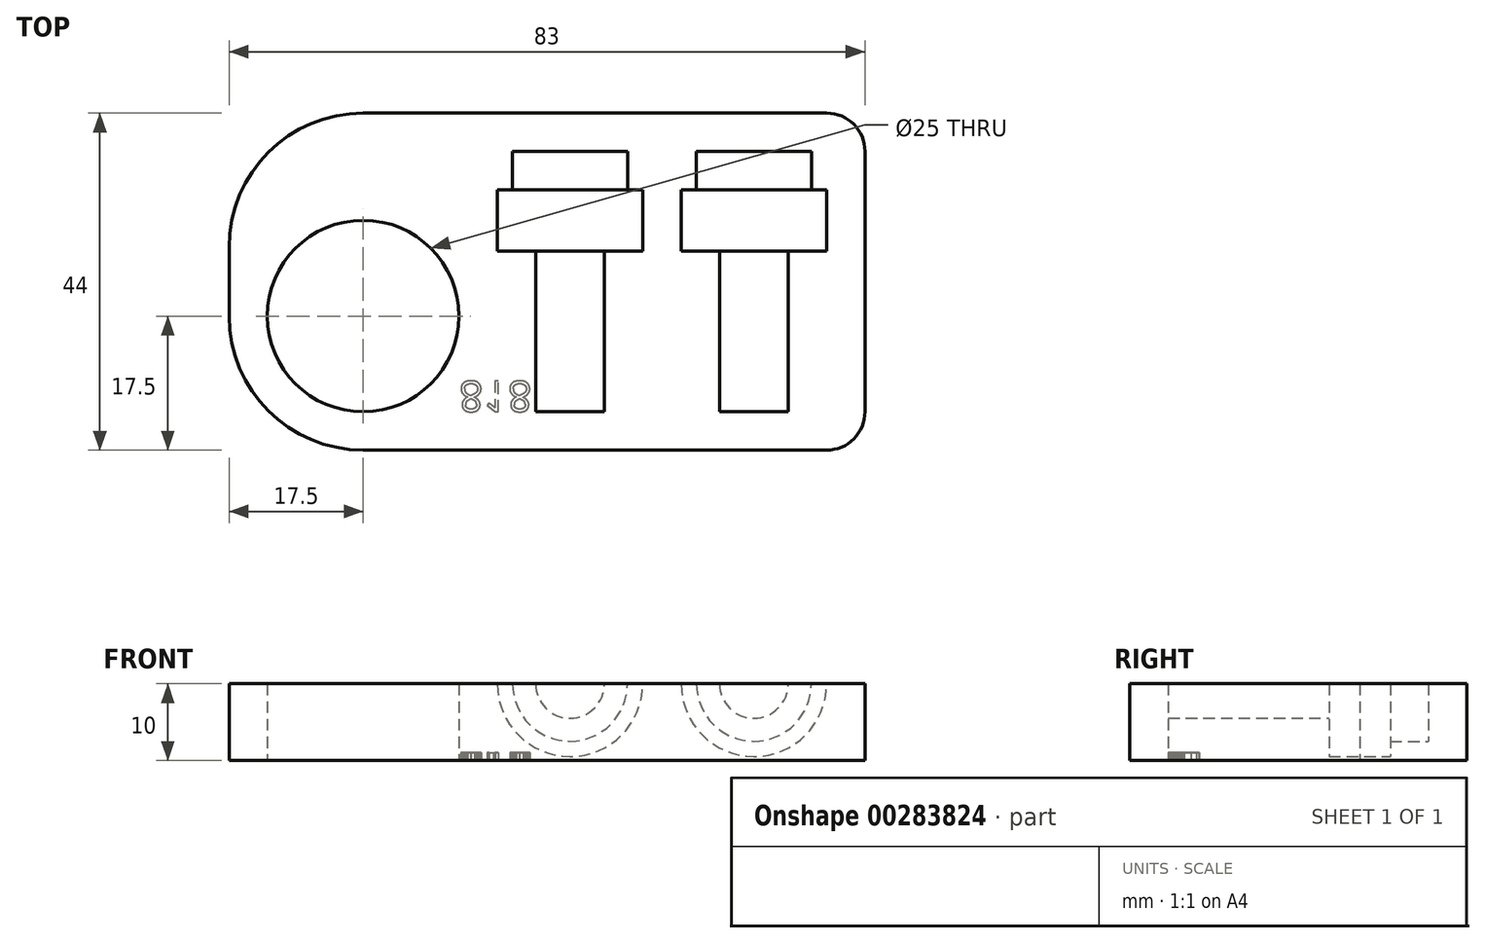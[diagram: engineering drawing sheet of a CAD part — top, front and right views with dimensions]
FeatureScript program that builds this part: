
annotation { "Feature Type Name" : "Feature", "Feature Type Description" : "" }
export const myFeature = defineFeature(function(context is Context, id is Id, definition is map)
    precondition{}
    {
        {
            var Q0;
            Q0=qCreatedBy(makeId("Top.planeOp"),FACE);
            var sketch = newSketch(context, id + "F0", { "sketchPlane" : qUnion([Q0])});
            skLineSegment(sketch, "E0.bottom", {"start": v(17.5, 0) * mm, "end": v(78, 0) * mm});
            skLineSegment(sketch, "E0.top", {"start": v(17.5, 44) * mm, "end": v(78, 44) * mm});
            skLineSegment(sketch, "E0.left", {"start": v(0, 17.5) * mm, "end": v(0, 26.5) * mm});
            skLineSegment(sketch, "E0.right", {"start": v(83, 5) * mm, "end": v(83, 39) * mm});
            skLineSegment(sketch, "E1.bottom", {"start": v(0, 0) * mm, "end": v(17.5, 0) * mm, "construction": true});
            skLineSegment(sketch, "E1.top", {"start": v(0, 17.5) * mm, "end": v(17.5, 17.5) * mm, "construction": true});
            skLineSegment(sketch, "E1.left", {"start": v(0, 0) * mm, "end": v(0, 17.5) * mm, "construction": true});
            skLineSegment(sketch, "E1.right", {"start": v(17.5, 0) * mm, "end": v(17.5, 17.5) * mm, "construction": true});
            skCircle(sketch, "E2", {"center": v(17.5, 17.5) * mm, "radius": 12.5 * mm});
            skPoint(sketch, "E3.visualSharp", {"position": v(0, 0) * mm});
            skArc(sketch, "E3.filletArc", {"start": v(0, 17.5) * mm, "mid": v(5.13, 5.13) * mm, "end": v(17.5, 0) * mm});
            skPoint(sketch, "E4.visualSharp", {"position": v(0, 44) * mm});
            skArc(sketch, "E4.filletArc", {"start": v(17.5, 44) * mm, "mid": v(5.13, 38.87) * mm, "end": v(0, 26.5) * mm});
            skPoint(sketch, "E5.visualSharp", {"position": v(83, 44) * mm});
            skArc(sketch, "E5.filletArc", {"start": v(83, 39) * mm, "mid": v(81.54, 42.54) * mm, "end": v(78, 44) * mm});
            skPoint(sketch, "E6.visualSharp", {"position": v(83, 0) * mm});
            skArc(sketch, "E6.filletArc", {"start": v(78, 0) * mm, "mid": v(81.54, 1.46) * mm, "end": v(83, 5) * mm});
            skSolve(sketch);
        }
        {
            var Q0;
            Q0=makeQuery(id+"F0.imprint","IMPRINT",FACE,{"disambiguationData":[TD([[makeQuery(id+"F0.imprint","IMPRINT",EDGE,{"derivedFrom":sQuery(id+"F0.wireOp",EDGE,"E0.bottom")}),1.0]])]});
            extrude(context, id + "F1", {"entities" : qUnion([Q0]), "depth" : 10 * mm});
        }
        {
            var Q0;
            Q0=makeQuery(id+"F1.opExtrude","CAP_FACE",FACE,{"disambiguationData":[OSD([sQuery(id+"F0.wireOp",EDGE,"E0.bottom"),sQuery(id+"F0.wireOp",EDGE,"E0.top"),sQuery(id+"F0.wireOp",EDGE,"E0.right"),sQuery(id+"F0.wireOp",EDGE,"E2"),sQuery(id+"F0.wireOp",EDGE,"E3.filletArc"),sQuery(id+"F0.wireOp",EDGE,"E4.filletArc"),sQuery(id+"F0.wireOp",EDGE,"E5.filletArc"),sQuery(id+"F0.wireOp",EDGE,"E6.filletArc")])],"isStart":false});
            var sketch = newSketch(context, id + "F2", { "sketchPlane" : qUnion([Q0])});
            skLineSegment(sketch, "E7.bottom", {"start": v(0, 0) * mm, "end": v(44.5, 0) * mm, "construction": true});
            skLineSegment(sketch, "E7.top", {"start": v(0, 5) * mm, "end": v(44.5, 5) * mm, "construction": true});
            skLineSegment(sketch, "E7.left", {"start": v(0, 0) * mm, "end": v(0, 5) * mm, "construction": true});
            skLineSegment(sketch, "E7.right", {"start": v(44.5, 0) * mm, "end": v(44.5, 5) * mm, "construction": true});
            skLineSegment(sketch, "E8.bottom", {"start": v(44.5, 5) * mm, "end": v(49, 5) * mm});
            skLineSegment(sketch, "E8.left", {"start": v(44.5, 5) * mm, "end": v(44.5, 26) * mm});
            skLineSegment(sketch, "E8.right", {"start": v(49, 5) * mm, "end": v(49, 26) * mm});
            skLineSegment(sketch, "E9.bottom", {"start": v(49, 26) * mm, "end": v(54, 26) * mm});
            skLineSegment(sketch, "E9.top", {"start": v(52, 34) * mm, "end": v(54, 34) * mm});
            skLineSegment(sketch, "E9.left", {"start": v(44.5, 26) * mm, "end": v(44.5, 34) * mm});
            skLineSegment(sketch, "E9.right", {"start": v(54, 26) * mm, "end": v(54, 34) * mm});
            skLineSegment(sketch, "E10.top", {"start": v(44.5, 39) * mm, "end": v(52, 39) * mm});
            skLineSegment(sketch, "E10.left", {"start": v(44.5, 34) * mm, "end": v(44.5, 39) * mm});
            skLineSegment(sketch, "E10.right", {"start": v(52, 34) * mm, "end": v(52, 39) * mm});
            skLineSegment(sketch, "E11", {"start": v(44.5, 5) * mm, "end": v(68.5, 5) * mm, "construction": true});
            skLineSegment(sketch, "E12.bottom", {"start": v(68.5, 5) * mm, "end": v(73, 5) * mm});
            skLineSegment(sketch, "E12.left", {"start": v(68.5, 5) * mm, "end": v(68.5, 26) * mm});
            skLineSegment(sketch, "E12.right", {"start": v(73, 5) * mm, "end": v(73, 26) * mm});
            skLineSegment(sketch, "E13.bottom", {"start": v(73, 26) * mm, "end": v(78, 26) * mm});
            skLineSegment(sketch, "E13.top", {"start": v(76, 34) * mm, "end": v(78, 34) * mm});
            skLineSegment(sketch, "E13.left", {"start": v(68.5, 26) * mm, "end": v(68.5, 34) * mm});
            skLineSegment(sketch, "E13.right", {"start": v(78, 26) * mm, "end": v(78, 34) * mm});
            skLineSegment(sketch, "E14.top", {"start": v(68.5, 39) * mm, "end": v(76, 39) * mm});
            skLineSegment(sketch, "E14.left", {"start": v(68.5, 34) * mm, "end": v(68.5, 39) * mm});
            skLineSegment(sketch, "E14.right", {"start": v(76, 34) * mm, "end": v(76, 39) * mm});
            skSolve(sketch);
        }
        {
            var Q0;
            Q0=makeQuery(id+"F2.imprint","IMPRINT",FACE,{"disambiguationData":[TD([[makeQuery(id+"F2.imprint","IMPRINT",EDGE,{"derivedFrom":sQuery(id+"F2.wireOp",EDGE,"E8.bottom")}),1.0]])]});
            var Q1;
            Q1=sQuery(id+"F2.wireOp",EDGE,"E8.left");
            revolve(context, id + "F3", {"operationType" : NewBodyOperationType.REMOVE, "entities" : qUnion([Q0]), "axis" : qUnion([Q1]), "revolveType" : RevolveType.FULL, "oppositeDirection" : true});
        }
        {
            var Q0;
            Q0=makeQuery(id+"F2.imprint","IMPRINT",FACE,{"disambiguationData":[TD([[makeQuery(id+"F2.imprint","IMPRINT",EDGE,{"derivedFrom":sQuery(id+"F2.wireOp",EDGE,"E12.bottom")}),1.0]])]});
            var Q1;
            Q1=sQuery(id+"F2.wireOp",EDGE,"E12.left");
            revolve(context, id + "F4", {"operationType" : NewBodyOperationType.REMOVE, "entities" : qUnion([Q0]), "axis" : qUnion([Q1]), "revolveType" : RevolveType.FULL, "oppositeDirection" : true});
        }
        {
            var Q0;
            Q0=makeQuery(id+"F1.opExtrude","CAP_FACE",FACE,{"disambiguationData":[OSD([sQuery(id+"F0.wireOp",EDGE,"E0.bottom"),sQuery(id+"F0.wireOp",EDGE,"E0.top"),sQuery(id+"F0.wireOp",EDGE,"E0.left"),sQuery(id+"F0.wireOp",EDGE,"E0.right"),sQuery(id+"F0.wireOp",EDGE,"E2"),sQuery(id+"F0.wireOp",EDGE,"E3.filletArc"),sQuery(id+"F0.wireOp",EDGE,"E4.filletArc"),sQuery(id+"F0.wireOp",EDGE,"E5.filletArc"),sQuery(id+"F0.wireOp",EDGE,"E6.filletArc")])],"isStart":true});
            var sketch = newSketch(context, id + "F5", { "sketchPlane" : qUnion([Q0])});
            skLineSegment(sketch, "E15.bottom", {"start": v(0, 0) * mm, "end": v(30, 0) * mm, "construction": true});
            skLineSegment(sketch, "E15.top", {"start": v(0, -5) * mm, "end": v(30, -5) * mm, "construction": true});
            skLineSegment(sketch, "E15.left", {"start": v(0, 0) * mm, "end": v(0, -5) * mm, "construction": true});
            skLineSegment(sketch, "E15.right", {"start": v(30, 0) * mm, "end": v(30, -5) * mm, "construction": true});
            skText(sketch, "E16", { "text": "818", "fontName": "OpenSans-Regular.ttf"});
            const initialGuessF5  = {"E16": [0.03, -0.009, 1, 0, 0.004]};
            skSetInitialGuess(sketch, initialGuessF5);
            skSolve(sketch);
        }
        {
            var Q0;
            Q0 = qSketchRegion(id + "F5", true);
            extrude(context, id + "F6", {"entities" : qUnion([Q0]), "operationType" : NewBodyOperationType.REMOVE, "oppositeDirection" : true, "depth" : 1 * mm});
        }
    });
